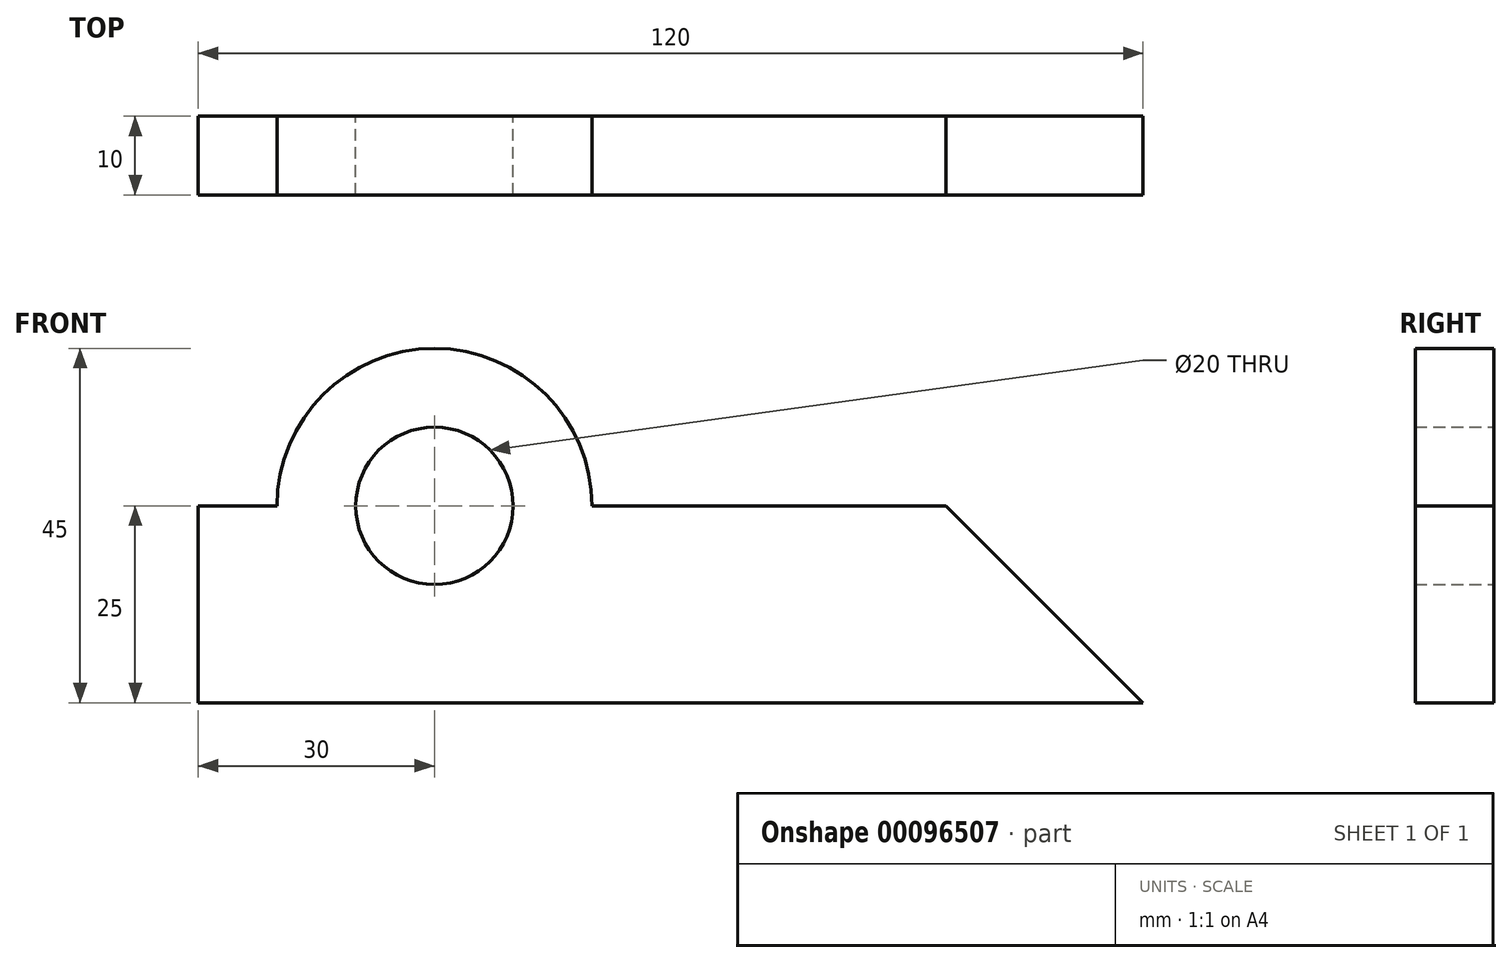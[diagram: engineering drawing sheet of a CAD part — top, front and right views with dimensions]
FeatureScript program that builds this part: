
annotation { "Feature Type Name" : "Feature", "Feature Type Description" : "" }
export const myFeature = defineFeature(function(context is Context, id is Id, definition is map)
    precondition{}
    {
        {
            var Q0;
            Q0=qCreatedBy(makeId("Front.planeOp"),FACE);
            var sketch = newSketch(context, id + "F0", { "sketchPlane" : qUnion([Q0])});
            skLineSegment(sketch, "E0", {"start": v(0, 0) * mm, "end": v(120, 0) * mm});
            skLineSegment(sketch, "E1", {"start": v(120, 0) * mm, "end": v(95, 25) * mm});
            skLineSegment(sketch, "E2", {"start": v(95, 25) * mm, "end": v(50, 25) * mm});
            skLineSegment(sketch, "E3", {"start": v(0, 25) * mm, "end": v(0, 0) * mm});
            skLineSegment(sketch, "E4", {"start": v(0, 25) * mm, "end": v(10, 25) * mm});
            skCircle(sketch, "E5", {"center": v(30, 25) * mm, "radius": 10 * mm});
            skArc(sketch, "E6", {"start": v(50, 25) * mm, "mid": v(30, 45) * mm, "end": v(10, 25) * mm});
            skSolve(sketch);
        }
        {
            var Q0;
            Q0=makeQuery(id+"F0.imprint","IMPRINT",FACE,{"disambiguationData":[TD([[makeQuery(id+"F0.imprint","IMPRINT",EDGE,{"derivedFrom":sQuery(id+"F0.wireOp",EDGE,"E0")}),1.0]])]});
            extrude(context, id + "F1", {"entities" : qUnion([Q0]), "depth" : 10 * mm});
        }
    });
